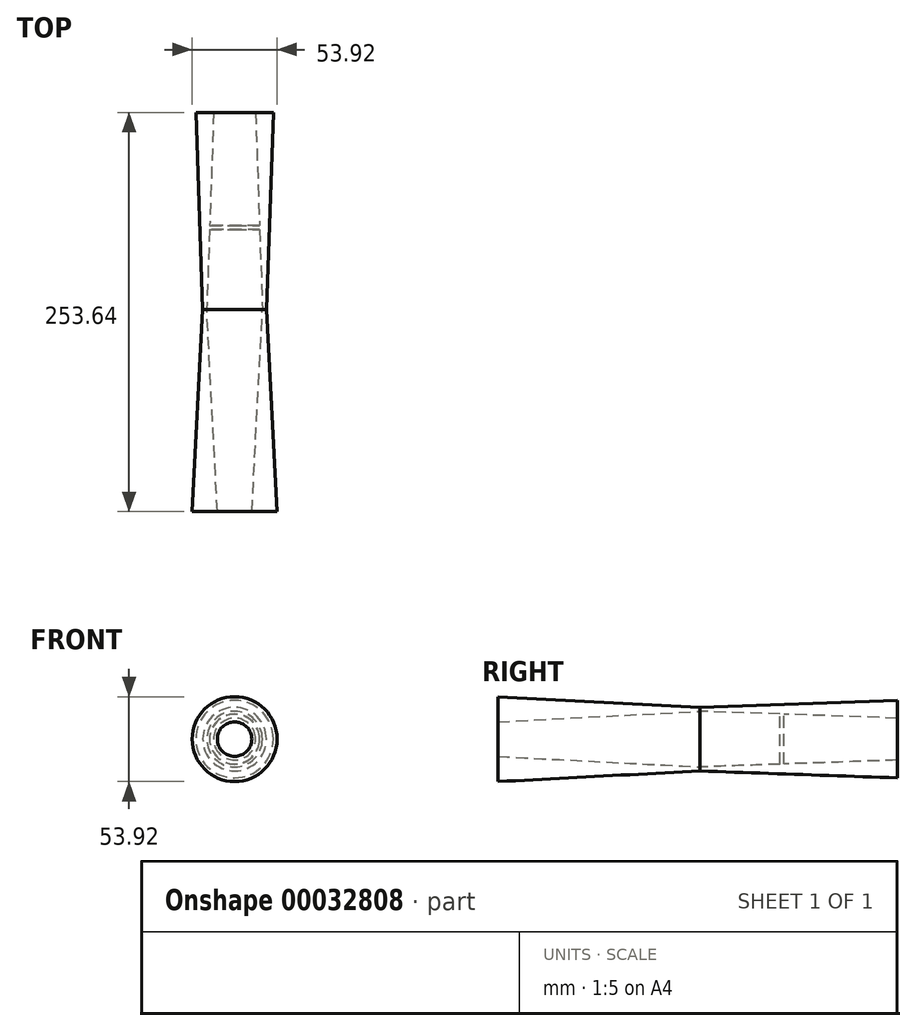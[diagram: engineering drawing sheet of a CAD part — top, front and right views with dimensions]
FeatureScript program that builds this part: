
annotation { "Feature Type Name" : "Feature", "Feature Type Description" : "" }
export const myFeature = defineFeature(function(context is Context, id is Id, definition is map)
    precondition{}
    {
        {
            var Q0;
            Q0=qCreatedBy(makeId("Front.planeOp"),FACE);
            var sketch = newSketch(context, id + "F0", { "sketchPlane" : qUnion([Q0])});
            skCircle(sketch, "E0", {"center": v(0, 0) * mm, "radius": 17.69 * mm});
            skSolve(sketch);
        }
        {
            var Q0;
            Q0=makeQuery(id+"F0.imprint","IMPRINT",FACE,{"disambiguationData":[TD([[makeQuery(id+"F0.imprint","IMPRINT",EDGE,{"derivedFrom":sQuery(id+"F0.wireOp",EDGE,"E0")}),1.0]])]});
            extrude(context, id + "F1", {"entities" : qUnion([Q0]), "endBound" : BoundingType.SYMMETRIC, "depth" : 50.8 * mm});
        }
        {
            var Q0;
            Q0=makeQuery(id+"F1.opExtrude","CAP_FACE",FACE,{"disambiguationData":[OSD([sQuery(id+"F0.wireOp",EDGE,"E0")])],"isStart":false});
            var Q1;
            Q1=makeQuery(id+"F1.opExtrude","SWEPT_BODY",BODY,{"disambiguationData":[OSD([sQuery(id+"F0.wireOp",EDGE,"E0")])]});
            shell(context, id + "F2", {"entities" : qUnion([Q0]), "parts" : qUnion([Q1]), "thickness" : 2.54 * mm, "oppositeDirection" : true});
        }
        {
            var Q0;
            Q0=makeQuery(id+"F1.opExtrude","CAP_FACE",FACE,{"disambiguationData":[OSD([sQuery(id+"F0.wireOp",EDGE,"E0")])],"isStart":false});
            extrude(context, id + "F3", {"entities" : qUnion([Q0]), "operationType" : NewBodyOperationType.ADD, "depth" : 128.4 * mm, "hasDraft" : true, "draftAngle" : 3 * degree, "hasSecondDirection" : true, "secondDirectionOppositeDirection" : true, "secondDirectionDepth" : 125.23 * mm, "hasSecondDirectionDraft" : true, "secondDirectionDraftAngle" : 2 * degree});
        }
        {
            var Q0;
            Q0=qCreatedBy(makeId("Front.planeOp"),FACE);
            var sketch = newSketch(context, id + "F4", { "sketchPlane" : qUnion([Q0])});
            skFitSpline(sketch, "E1", {"points": [v(-67.83, 35.44) * mm, v(-54.56, 69.24) * mm, v(-42.3, 41.12) * mm, v(-34.13, 67.67) * mm, v(-14.25, 44.42) * mm, v(-10.53, 65.88) * mm, v(8.53, 44.3) * mm, v(16.17, 61.21) * mm, v(29.08, 47.31) * mm, v(42.12, 61.12) * mm, v(56.54, 49.64) * mm, v(66.94, 61.74) * mm, v(72.98, 49.97) * mm], "startDerivative": vector(119.58, 551.36) * mm, "endDerivative": vector(84.82, -307.36) * mm});
            skLineSegment(sketch, "E2", {"start": v(-67.51, 70.37) * mm, "end": v(84.25, 61.84) * mm, "construction": true});
            skSolve(sketch);
        }
        {
            var Q0;
            Q0=sQuery(id+"F4.wireOp",EDGE,"E1");
            extrude(context, id + "F5", {"bodyType" : ToolBodyType.SURFACE, "surfaceEntities" : qUnion([Q0]), "endBound" : BoundingType.SYMMETRIC, "depth" : 25.4 * mm});
        }
    });
